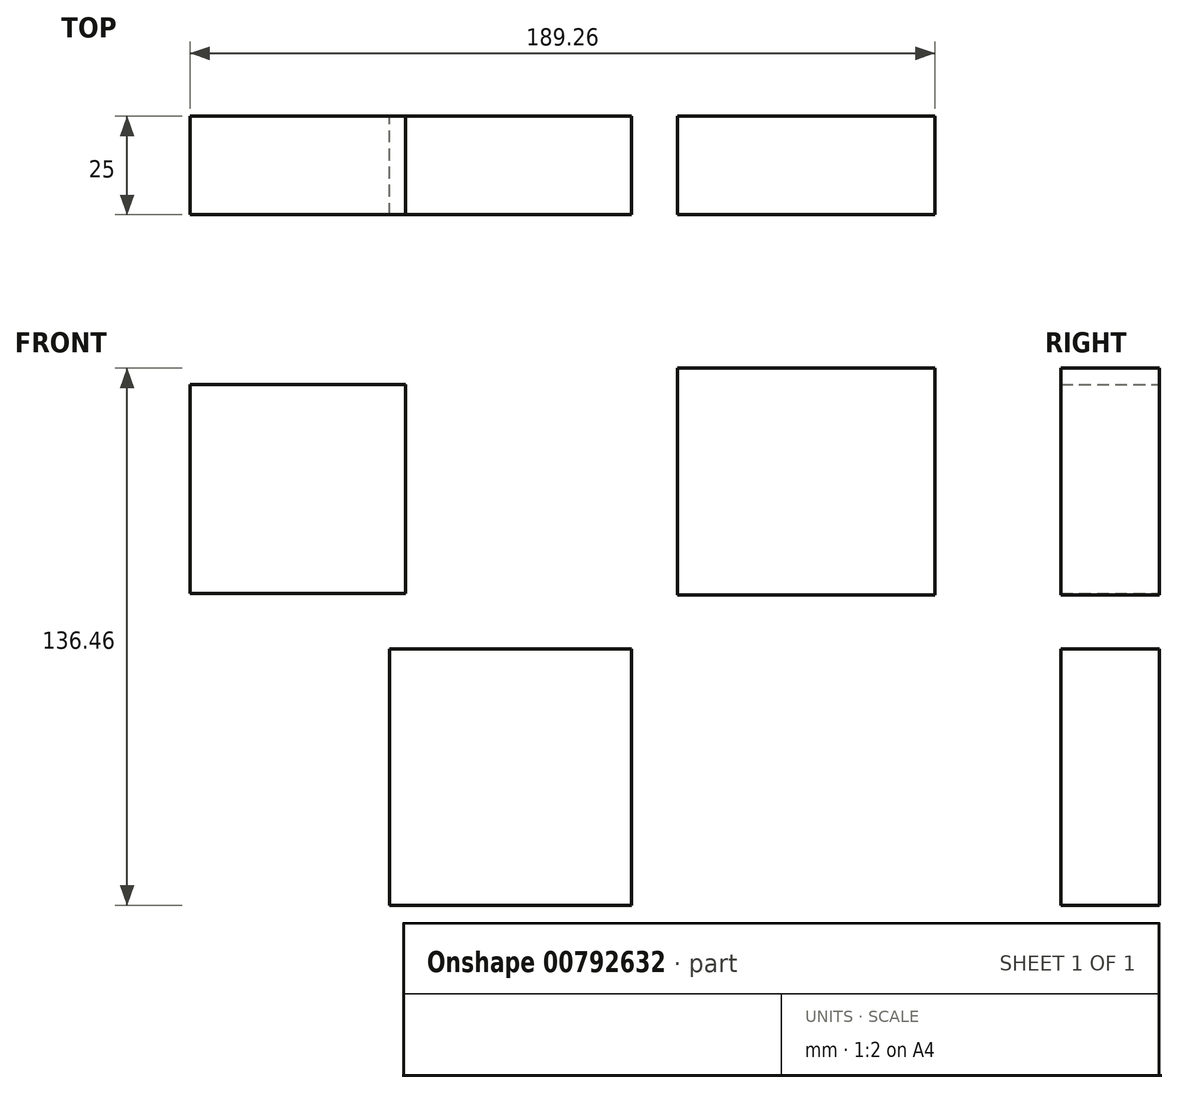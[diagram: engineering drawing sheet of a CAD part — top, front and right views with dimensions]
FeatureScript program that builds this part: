
annotation { "Feature Type Name" : "Feature", "Feature Type Description" : "" }
export const myFeature = defineFeature(function(context is Context, id is Id, definition is map)
    precondition{}
    {
        {
            var Q0;
            Q0=qCreatedBy(makeId("Front.planeOp"),FACE);
            var sketch = newSketch(context, id + "F0", { "sketchPlane" : qUnion([Q0])});
            skLineSegment(sketch, "E0.bottom", {"start": v(-99.3, 31.58) * mm, "end": v(-44.56, 31.58) * mm});
            skLineSegment(sketch, "E0.top", {"start": v(-99.3, 84.77) * mm, "end": v(-44.56, 84.77) * mm});
            skLineSegment(sketch, "E0.left", {"start": v(-99.3, 31.58) * mm, "end": v(-99.3, 84.77) * mm});
            skLineSegment(sketch, "E0.right", {"start": v(-44.56, 31.58) * mm, "end": v(-44.56, 84.77) * mm});
            skPoint(sketch, "E0.middle", {"position": v(-71.93, 58.18) * mm});
            skLineSegment(sketch, "E1.bottom", {"start": v(24.53, 31.28) * mm, "end": v(89.96, 31.28) * mm});
            skLineSegment(sketch, "E1.top", {"start": v(24.53, 88.89) * mm, "end": v(89.96, 88.89) * mm});
            skLineSegment(sketch, "E1.left", {"start": v(24.53, 31.28) * mm, "end": v(24.53, 88.89) * mm});
            skLineSegment(sketch, "E1.right", {"start": v(89.96, 31.28) * mm, "end": v(89.96, 88.89) * mm});
            skPoint(sketch, "E1.middle", {"position": v(57.24, 60.08) * mm});
            skLineSegment(sketch, "E2.bottom", {"start": v(-48.57, -47.57) * mm, "end": v(12.85, -47.57) * mm});
            skLineSegment(sketch, "E2.top", {"start": v(-48.57, 17.56) * mm, "end": v(12.85, 17.56) * mm});
            skLineSegment(sketch, "E2.left", {"start": v(-48.57, -47.57) * mm, "end": v(-48.57, 17.56) * mm});
            skLineSegment(sketch, "E2.right", {"start": v(12.85, -47.57) * mm, "end": v(12.85, 17.56) * mm});
            skPoint(sketch, "E2.middle", {"position": v(-17.86, -15) * mm});
            skSolve(sketch);
        }
        {
            var Q0;
            Q0=makeQuery(id+"F0.imprint","IMPRINT",FACE,{"disambiguationData":[TD([[makeQuery(id+"F0.imprint","IMPRINT",EDGE,{"derivedFrom":sQuery(id+"F0.wireOp",EDGE,"E2.bottom")}),1.0]])]});
            var Q1;
            Q1=makeQuery(id+"F0.imprint","IMPRINT",FACE,{"disambiguationData":[TD([[makeQuery(id+"F0.imprint","IMPRINT",EDGE,{"derivedFrom":sQuery(id+"F0.wireOp",EDGE,"E1.bottom")}),1.0]])]});
            var Q2;
            Q2=makeQuery(id+"F0.imprint","IMPRINT",FACE,{"disambiguationData":[TD([[makeQuery(id+"F0.imprint","IMPRINT",EDGE,{"derivedFrom":sQuery(id+"F0.wireOp",EDGE,"E0.bottom")}),1.0]])]});
            extrude(context, id + "F1", {"entities" : qUnion([Q0, Q1, Q2]), "depth" : 25 * mm, "offsetDistance" : 25 * mm});
        }
    });
